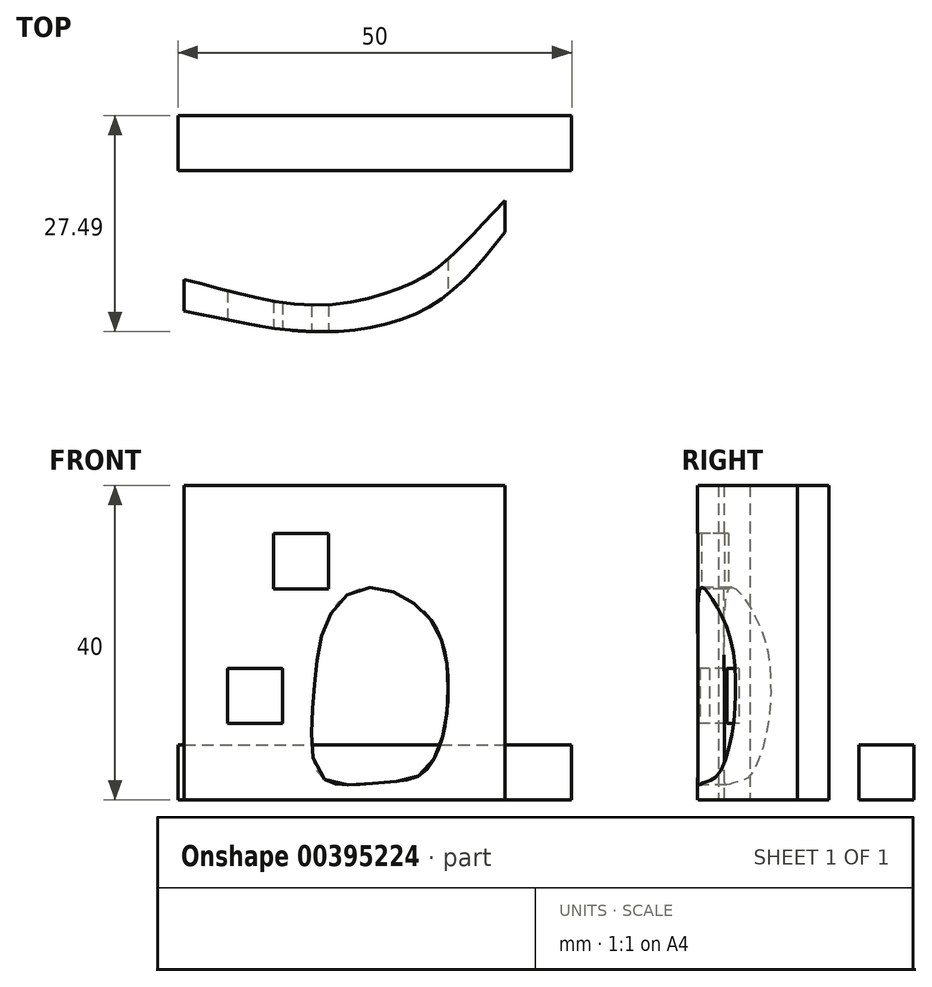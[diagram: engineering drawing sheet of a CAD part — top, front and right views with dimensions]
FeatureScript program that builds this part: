
annotation { "Feature Type Name" : "Feature", "Feature Type Description" : "" }
export const myFeature = defineFeature(function(context is Context, id is Id, definition is map)
    precondition{}
    {
        {
            var Q0;
            Q0=qCreatedBy(makeId("Top.planeOp"),FACE);
            var sketch = newSketch(context, id + "F0", { "sketchPlane" : qUnion([Q0])});
            skLineSegment(sketch, "E0", {"start": v(-48.62, 10.29) * mm, "end": v(-48.62, 6.29) * mm});
            skLineSegment(sketch, "E1", {"start": v(-7.83, 20.3) * mm, "end": v(-7.83, 16.3) * mm});
            skFitSpline(sketch, "E2", {"points": [v(-48.62, 6.29) * mm, v(-33.68, 3.73) * mm, v(-18.4, 6.29) * mm, v(-7.83, 16.3) * mm], "startDerivative": vector(43.78, -8.35) * mm, "endDerivative": vector(28.44, 37.19) * mm});
            skFitSpline(sketch, "E3", {"points": [v(-48.62, 10.29) * mm, v(-31.32, 7.01) * mm, v(-18.75, 10.29) * mm, v(-14.93, 13.02) * mm, v(-7.83, 20.3) * mm], "startDerivative": vector(48.37, -11.07) * mm, "endDerivative": vector(31.6, 33.76) * mm});
            skSolve(sketch);
        }
        {
            var Q0;
            Q0=makeQuery(id+"F0.imprint","IMPRINT",FACE,{"disambiguationData":[TD([[makeQuery(id+"F0.imprint","IMPRINT",EDGE,{"derivedFrom":sQuery(id+"F0.wireOp",EDGE,"E0")}),1.0]])]});
            extrude(context, id + "F1", {"entities" : qUnion([Q0]), "depth" : 40 * mm});
        }
        {
            var Q0;
            Q0=qCreatedBy(makeId("Front.planeOp"),FACE);
            var sketch = newSketch(context, id + "F2", { "sketchPlane" : qUnion([Q0])});
            skLineSegment(sketch, "E4.bottom", {"start": v(-43.05, 16.74) * mm, "end": v(-36.05, 16.74) * mm});
            skLineSegment(sketch, "E4.top", {"start": v(-43.05, 9.74) * mm, "end": v(-36.05, 9.74) * mm});
            skLineSegment(sketch, "E4.left", {"start": v(-43.05, 16.74) * mm, "end": v(-43.05, 9.74) * mm});
            skLineSegment(sketch, "E4.right", {"start": v(-36.05, 16.74) * mm, "end": v(-36.05, 9.74) * mm});
            skFitSpline(sketch, "E5", {"points": [v(-30.77, 2.64) * mm, v(-23.3, 2.28) * mm, v(-18.57, 3.19) * mm, v(-15.84, 7.74) * mm, v(-15.11, 16.3) * mm, v(-16.93, 22.49) * mm, v(-21.67, 26.31) * mm, v(-26.77, 26.67) * mm, v(-30.4, 22.85) * mm, v(-31.86, 16.11) * mm, v(-32.41, 8.47) * mm, v(-30.77, 2.64) * mm]});
            skLineSegment(sketch, "E6.bottom", {"start": v(-37.23, 33.86) * mm, "end": v(-30.23, 33.86) * mm});
            skLineSegment(sketch, "E6.top", {"start": v(-37.23, 26.86) * mm, "end": v(-30.23, 26.86) * mm});
            skLineSegment(sketch, "E6.left", {"start": v(-37.23, 33.86) * mm, "end": v(-37.23, 26.86) * mm});
            skLineSegment(sketch, "E6.right", {"start": v(-30.23, 33.86) * mm, "end": v(-30.23, 26.86) * mm});
            skSolve(sketch);
        }
        {
            var Q0;
            Q0=makeQuery(id+"F2.imprint","IMPRINT",FACE,{"disambiguationData":[TD([[makeQuery(id+"F2.imprint","IMPRINT",EDGE,{"derivedFrom":sQuery(id+"F2.wireOp",EDGE,"E4.bottom")}),-1.0]])]});
            var Q1;
            Q1=makeQuery(id+"F2.imprint","IMPRINT",FACE,{"disambiguationData":[TD([[makeQuery(id+"F2.imprint","IMPRINT",EDGE,{"derivedFrom":sQuery(id+"F2.wireOp",EDGE,"E6.bottom")}),-1.0]])]});
            var Q2;
            Q2=makeQuery(id+"F2.imprint","IMPRINT",FACE,{"disambiguationData":[TD([[makeQuery(id+"F2.imprint","IMPRINT",EDGE,{"derivedFrom":sQuery(id+"F2.wireOp",EDGE,"E5")}),1.0]])]});
            extrude(context, id + "F3", {"entities" : qUnion([Q0, Q1, Q2]), "operationType" : NewBodyOperationType.REMOVE, "oppositeDirection" : true, "depth" : 25 * mm});
        }
        {
            var Q0;
            Q0=qCreatedBy(makeId("Top.planeOp"),FACE);
            var sketch = newSketch(context, id + "F4", { "sketchPlane" : qUnion([Q0])});
            skLineSegment(sketch, "E7.bottom", {"start": v(-49.34, 24.13) * mm, "end": v(0.66, 24.13) * mm});
            skLineSegment(sketch, "E7.top", {"start": v(-49.34, 31.13) * mm, "end": v(0.66, 31.13) * mm});
            skLineSegment(sketch, "E7.left", {"start": v(-49.34, 24.13) * mm, "end": v(-49.34, 31.13) * mm});
            skLineSegment(sketch, "E7.right", {"start": v(0.66, 24.13) * mm, "end": v(0.66, 31.13) * mm});
            skSolve(sketch);
        }
        {
            var Q0;
            Q0=makeQuery(id+"F4.imprint","IMPRINT",FACE,{"disambiguationData":[TD([[makeQuery(id+"F4.imprint","IMPRINT",EDGE,{"derivedFrom":sQuery(id+"F4.wireOp",EDGE,"E7.bottom")}),1.0]])]});
            extrude(context, id + "F5", {"entities" : qUnion([Q0]), "depth" : 7 * mm});
        }
    });
